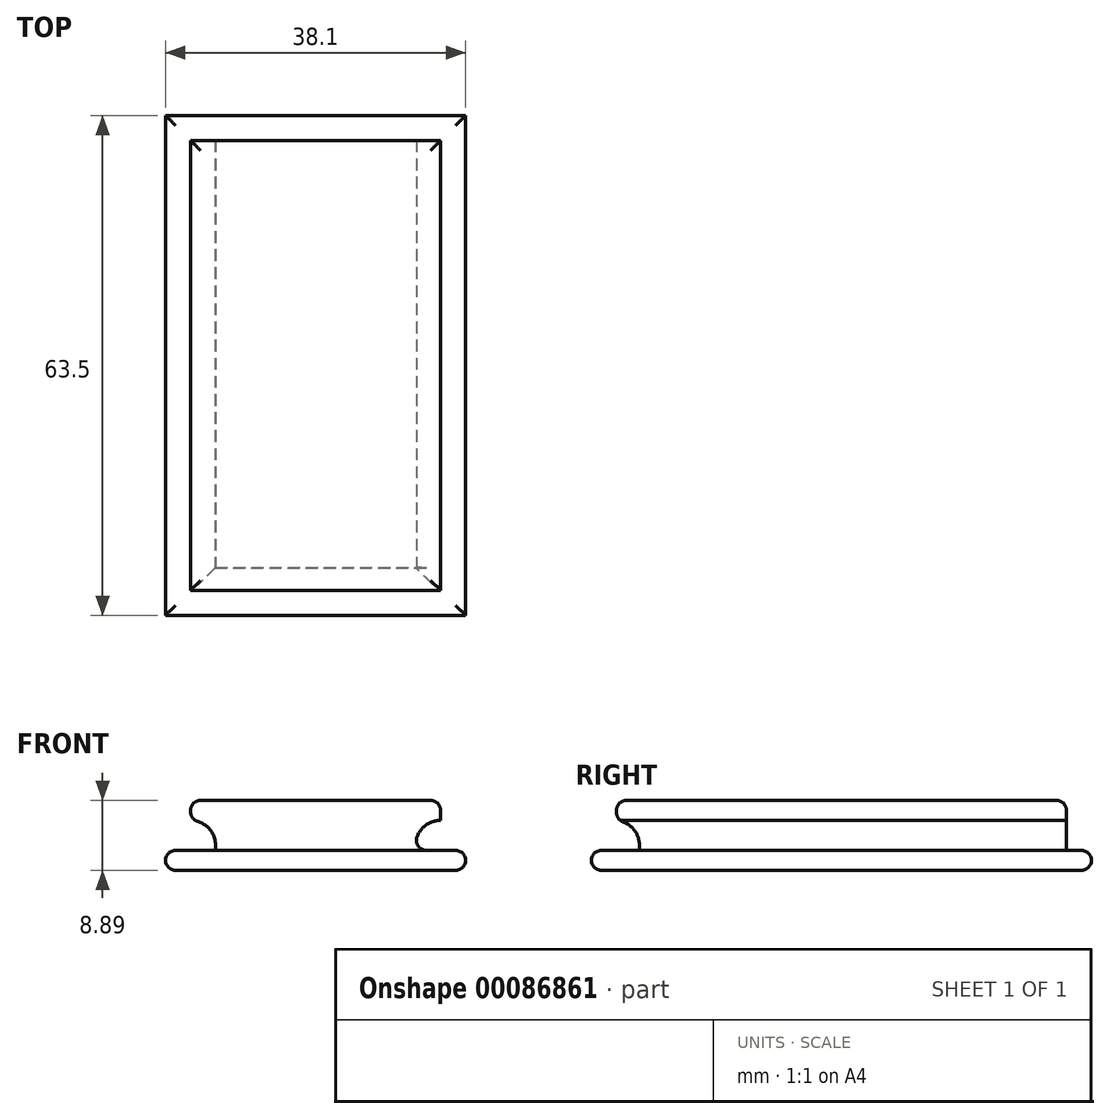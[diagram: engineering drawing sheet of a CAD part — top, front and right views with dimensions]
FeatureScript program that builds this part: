
annotation { "Feature Type Name" : "Feature", "Feature Type Description" : "" }
export const myFeature = defineFeature(function(context is Context, id is Id, definition is map)
    precondition{}
    {
        {
            var Q0;
            Q0=qCreatedBy(makeId("Top.planeOp"),FACE);
            var sketch = newSketch(context, id + "F0", { "sketchPlane" : qUnion([Q0])});
            skLineSegment(sketch, "E0.bottom", {"start": v(-25.4, 19.05) * mm, "end": v(25.4, 19.05) * mm});
            skLineSegment(sketch, "E0.top", {"start": v(-25.4, -19.05) * mm, "end": v(25.4, -19.05) * mm});
            skLineSegment(sketch, "E0.left", {"start": v(-31.75, 12.7) * mm, "end": v(-31.75, -12.7) * mm});
            skLineSegment(sketch, "E0.right", {"start": v(31.75, 12.7) * mm, "end": v(31.75, -12.7) * mm});
            skPoint(sketch, "E0.middle", {"position": v(0, 0) * mm});
            skPoint(sketch, "E1.visualSharp", {"position": v(-31.75, 19.05) * mm});
            skArc(sketch, "E1.filletArc", {"start": v(-25.4, 19.05) * mm, "mid": v(-29.9, 17.2) * mm, "end": v(-31.75, 12.7) * mm});
            skPoint(sketch, "E2.visualSharp", {"position": v(-31.75, -19.05) * mm});
            skArc(sketch, "E2.filletArc", {"start": v(-31.75, -12.7) * mm, "mid": v(-29.9, -17.2) * mm, "end": v(-25.4, -19.05) * mm});
            skPoint(sketch, "E3.visualSharp", {"position": v(31.75, 19.05) * mm});
            skArc(sketch, "E3.filletArc", {"start": v(31.75, 12.7) * mm, "mid": v(29.9, 17.2) * mm, "end": v(25.4, 19.05) * mm});
            skPoint(sketch, "E4.visualSharp", {"position": v(31.75, -19.05) * mm});
            skArc(sketch, "E4.filletArc", {"start": v(25.4, -19.05) * mm, "mid": v(29.9, -17.2) * mm, "end": v(31.75, -12.7) * mm});
            skSolve(sketch);
        }
        {
            var Q0;
            Q0=makeQuery(id+"F0.imprint","IMPRINT",FACE,{"disambiguationData":[TD([[makeQuery(id+"F0.imprint","IMPRINT",EDGE,{"derivedFrom":sQuery(id+"F0.wireOp",EDGE,"E0.bottom")}),-1.0]])]});
            extrude(context, id + "F1", {"entities" : qUnion([Q0]), "depth" : 7.62 * mm});
        }
        {
            var Q0;
            Q0=makeQuery(id+"F1.opExtrude","SWEPT_BODY",BODY,{"disambiguationData":[OSD([sQuery(id+"F0.wireOp",EDGE,"E0.bottom"),sQuery(id+"F0.wireOp",EDGE,"E0.top"),sQuery(id+"F0.wireOp",EDGE,"E0.left"),sQuery(id+"F0.wireOp",EDGE,"E0.right"),sQuery(id+"F0.wireOp",EDGE,"E1.filletArc"),sQuery(id+"F0.wireOp",EDGE,"E2.filletArc"),sQuery(id+"F0.wireOp",EDGE,"E3.filletArc"),sQuery(id+"F0.wireOp",EDGE,"E4.filletArc")])]});
            deleteBodies(context, id + "F2", {"entities" : qUnion([Q0])});
        }
        {
            var Q0;
            Q0=qCreatedBy(makeId("Top.planeOp"),FACE);
            var sketch = newSketch(context, id + "F3", { "sketchPlane" : qUnion([Q0])});
            skLineSegment(sketch, "E5.bottom", {"start": v(-15.87, 28.58) * mm, "end": v(15.88, 28.58) * mm});
            skLineSegment(sketch, "E5.top", {"start": v(-15.88, -28.58) * mm, "end": v(15.87, -28.58) * mm});
            skLineSegment(sketch, "E5.left", {"start": v(-15.87, 28.58) * mm, "end": v(-15.88, -28.58) * mm});
            skLineSegment(sketch, "E5.right", {"start": v(15.88, 28.58) * mm, "end": v(15.87, -28.58) * mm});
            skPoint(sketch, "E5.middle", {"position": v(0, 0) * mm});
            skSolve(sketch);
        }
        {
            var Q0;
            Q0=makeQuery(id+"F3.imprint","IMPRINT",FACE,{"disambiguationData":[TD([[makeQuery(id+"F3.imprint","IMPRINT",EDGE,{"derivedFrom":sQuery(id+"F3.wireOp",EDGE,"E5.bottom")}),-1.0]])]});
            extrude(context, id + "F4", {"entities" : qUnion([Q0]), "depth" : 6.35 * mm});
        }
        {
            var Q0;
            Q0=makeQuery(id+"F4.opExtrude","SWEPT_FACE",FACE,{"disambiguationData":[OSD([sQuery(id+"F3.wireOp",EDGE,"E5.top")])]});
            var sketch = newSketch(context, id + "F5", { "sketchPlane" : qUnion([Q0])});
            skCircle(sketch, "E6", {"center": v(15.87, 3.18) * mm, "radius": 3.18 * mm});
            skCircle(sketch, "E7.MirrorC", {"center": v(-15.87, 3.18) * mm, "radius": 3.18 * mm});
            skSolve(sketch);
        }
        {
            var Q0;
            {var subQ1=sQuery(id+"F3.wireOp",EDGE,"E5.top");var subQ2=makeQuery(id+"F4.opExtrude","SWEPT_EDGE",EDGE,{"disambiguationData":[OSD([subQ1,sQuery(id+"F3.wireOp",EDGE,"E5.left")])]});Q0=makeQuery(id+"F5.imprint","IMPRINT",FACE,{"disambiguationData":[TD([[makeQuery(id+"F5.imprint","IMPRINT",EDGE,{"derivedFrom":subQ2}),1.0]])]});}
            var Q1;
            {var subQ1=sQuery(id+"F3.wireOp",EDGE,"E5.top");var subQ2=makeQuery(id+"F4.opExtrude","SWEPT_EDGE",EDGE,{"disambiguationData":[OSD([subQ1,sQuery(id+"F3.wireOp",EDGE,"E5.right")])]});Q1=makeQuery(id+"F5.imprint","IMPRINT",FACE,{"disambiguationData":[TD([[makeQuery(id+"F5.imprint","IMPRINT",EDGE,{"derivedFrom":subQ2}),-1.0]])]});}
            extrude(context, id + "F6", {"entities" : qUnion([Q0, Q1]), "operationType" : NewBodyOperationType.REMOVE, "endBound" : BoundingType.THROUGH_ALL, "oppositeDirection" : true, "depth" : 25.4 * mm});
        }
        {
            var Q0;
            Q0=makeQuery(id+"F4.opExtrude","SWEPT_FACE",FACE,{"disambiguationData":[OSD([sQuery(id+"F3.wireOp",EDGE,"E5.left")])]});
            var sketch = newSketch(context, id + "F7", { "sketchPlane" : qUnion([Q0])});
            skSolve(sketch);
        }
        {
            var Q0;
            Q0=qCreatedBy(makeId("Right.planeOp"),FACE);
            cPlane(context, id + "F8", {"entities" : qUnion([Q0]), "cplaneType" : CPlaneType.OFFSET, "offset" : 152.4 * mm, "width" : 152.4 * mm, "height" : 152.4 * mm});
        }
        {
            var Q0;
            Q0=qCreatedBy(id+"F8.planeOp",FACE);
            var sketch = newSketch(context, id + "F9", { "sketchPlane" : qUnion([Q0])});
            skCircle(sketch, "E8", {"center": v(-28.83, 3.18) * mm, "radius": 3.17 * mm});
            skCircle(sketch, "E9.MirrorC", {"center": v(28.83, 3.18) * mm, "radius": 3.17 * mm});
            skSolve(sketch);
        }
        {
            var Q0;
            Q0=makeQuery(id+"F9.imprint","IMPRINT",FACE,{"disambiguationData":[TD([[makeQuery(id+"F9.imprint","IMPRINT",EDGE,{"derivedFrom":sQuery(id+"F9.wireOp",EDGE,"E8")}),1.0]])]});
            var Q1;
            Q1=makeQuery(id+"F9.imprint","IMPRINT",FACE,{"disambiguationData":[TD([[makeQuery(id+"F9.imprint","IMPRINT",EDGE,{"derivedFrom":sQuery(id+"F9.wireOp",EDGE,"E9.MirrorC")}),-1.0]])]});
            extrude(context, id + "F10", {"entities" : qUnion([Q0, Q1]), "operationType" : NewBodyOperationType.REMOVE, "endBound" : BoundingType.THROUGH_ALL, "oppositeDirection" : true, "depth" : 25.4 * mm});
        }
        {
            var Q0;
            Q0=qCreatedBy(makeId("Top.planeOp"),FACE);
            var sketch = newSketch(context, id + "F11", { "sketchPlane" : qUnion([Q0])});
            skLineSegment(sketch, "E10.bottom", {"start": v(-19.05, 31.75) * mm, "end": v(19.05, 31.75) * mm});
            skLineSegment(sketch, "E10.top", {"start": v(-19.05, -31.75) * mm, "end": v(19.05, -31.75) * mm});
            skLineSegment(sketch, "E10.left", {"start": v(-19.05, 31.75) * mm, "end": v(-19.05, -31.75) * mm});
            skLineSegment(sketch, "E10.right", {"start": v(19.05, 31.75) * mm, "end": v(19.05, -31.75) * mm});
            skPoint(sketch, "E10.middle", {"position": v(0, 0) * mm});
            skSolve(sketch);
        }
        {
            var Q0;
            Q0=makeQuery(id+"F11.imprint","IMPRINT",FACE,{"disambiguationData":[TD([[makeQuery(id+"F11.imprint","IMPRINT",EDGE,{"derivedFrom":sQuery(id+"F11.wireOp",EDGE,"E10.bottom")}),-1.0]])]});
            extrude(context, id + "F12", {"entities" : qUnion([Q0]), "operationType" : NewBodyOperationType.ADD, "depth" : 2.54 * mm});
        }
        {
            var Q0;
            Q0=makeQuery(id+"F4.opExtrude","CAP_FACE",FACE,{"disambiguationData":[OSD([sQuery(id+"F3.wireOp",EDGE,"E5.bottom"),sQuery(id+"F3.wireOp",EDGE,"E5.top"),sQuery(id+"F3.wireOp",EDGE,"E5.left"),sQuery(id+"F3.wireOp",EDGE,"E5.right")])],"isStart":false});
            extrude(context, id + "F13", {"entities" : qUnion([Q0]), "operationType" : NewBodyOperationType.ADD, "depth" : 2.54 * mm});
        }
        {
            var Q0;
            Q0=makeQuery(id+"F13.opExtrude","CAP_EDGE",EDGE,{"disambiguationData":[OSD([sQuery(id+"F3.wireOp",EDGE,"E5.top")])],"isStart":false});
            var Q1;
            Q1=makeQuery(id+"F10.boolean.opBoolean","INTERSECT",EDGE,{"disambiguationData":[OD(1.0)],"derivedFrom":[makeQuery(id+"F4.opExtrude","SWEPT_FACE",FACE,{"disambiguationData":[OSD([sQuery(id+"F3.wireOp",EDGE,"E5.top")])]}),makeQuery(id+"F10.opExtrude","SWEPT_FACE",FACE,{"disambiguationData":[OSD([sQuery(id+"F9.wireOp",EDGE,"E8")])]})]});
            var Q2;
            Q2=makeQuery(id+"F13.opExtrude","CAP_EDGE",EDGE,{"disambiguationData":[OSD([sQuery(id+"F3.wireOp",EDGE,"E5.top"),sQuery(id+"F3.wireOp",EDGE,"E5.right"),sQuery(id+"F5.wireOp",EDGE,"E6")])],"isStart":false});
            var Q3;
            Q3=makeQuery(id+"F12.boolean.opBoolean","INTERSECT",EDGE,{"derivedFrom":[makeQuery(id+"F6.boolean.opBoolean","COPY",FACE,{"derivedFrom":makeQuery(id+"F6.opExtrude","SWEPT_FACE",FACE,{"disambiguationData":[OSD([sQuery(id+"F5.wireOp",EDGE,"E6")])]})}),makeQuery(id+"F12.opExtrude","CAP_FACE",FACE,{"disambiguationData":[OSD([sQuery(id+"F11.wireOp",EDGE,"E10.bottom"),sQuery(id+"F11.wireOp",EDGE,"E10.top"),sQuery(id+"F11.wireOp",EDGE,"E10.left"),sQuery(id+"F11.wireOp",EDGE,"E10.right")])],"isStart":false})]});
            var Q4;
            Q4=makeQuery(id+"F13.opExtrude","CAP_EDGE",EDGE,{"disambiguationData":[OSD([sQuery(id+"F3.wireOp",EDGE,"E5.bottom")])],"isStart":false});
            var Q5;
            Q5=makeQuery(id+"F13.opExtrude","CAP_EDGE",EDGE,{"disambiguationData":[OSD([sQuery(id+"F3.wireOp",EDGE,"E5.top"),sQuery(id+"F3.wireOp",EDGE,"E5.left"),sQuery(id+"F5.wireOp",EDGE,"E7.MirrorC")])],"isStart":false});
            var Q6;
            Q6=makeQuery(id+"F12.opExtrude","CAP_EDGE",EDGE,{"disambiguationData":[OSD([sQuery(id+"F11.wireOp",EDGE,"E10.top")])],"isStart":false});
            var Q7;
            Q7=makeQuery(id+"F12.opExtrude","CAP_EDGE",EDGE,{"disambiguationData":[OSD([sQuery(id+"F11.wireOp",EDGE,"E10.right")])],"isStart":false});
            var Q8;
            Q8=makeQuery(id+"F12.opExtrude","CAP_EDGE",EDGE,{"disambiguationData":[OSD([sQuery(id+"F11.wireOp",EDGE,"E10.right")])],"isStart":true});
            var Q9;
            Q9=makeQuery(id+"F12.opExtrude","CAP_EDGE",EDGE,{"disambiguationData":[OSD([sQuery(id+"F11.wireOp",EDGE,"E10.top")])],"isStart":true});
            var Q10;
            {var subQ0=sQuery(id+"F5.wireOp",EDGE,"E7.MirrorC");var subQ1=sQuery(id+"F3.wireOp",EDGE,"E5.left");var subQ2=sQuery(id+"F3.wireOp",EDGE,"E5.top");Q10=makeQuery(id+"F13.boolean.opBoolean","MERGE",EDGE,{"derivedFrom":[makeQuery(id+"F6.boolean.opBoolean","MERGE",EDGE,{"derivedFrom":[makeQuery(id+"F4.opExtrude","CAP_EDGE",EDGE,{"disambiguationData":[OSD([subQ1])],"isStart":false}),makeQuery(id+"F6.opExtrude","SWEPT_EDGE",EDGE,{"disambiguationData":[OSD([subQ2,subQ1,subQ0]),TDD([makeQuery(id+"F5.imprint","INTERSECT",VERTEX,{"derivedFrom":[makeQuery(id+"F4.opExtrude","SWEPT_EDGE",EDGE,{"disambiguationData":[OSD([subQ2,subQ1])]}),makeQuery(id+"F4.opExtrude","CAP_EDGE",EDGE,{"disambiguationData":[OSD([subQ2])],"isStart":false}),subQ0]})])]})]}),makeQuery(id+"F13.opExtrude","CAP_EDGE",EDGE,{"disambiguationData":[OSD([subQ2,subQ1,subQ0])],"isStart":true})]});}
            var Q11;
            Q11=makeQuery(id+"F12.opExtrude","CAP_EDGE",EDGE,{"disambiguationData":[OSD([sQuery(id+"F11.wireOp",EDGE,"E10.left")])],"isStart":false});
            var Q12;
            Q12=makeQuery(id+"F12.opExtrude","CAP_EDGE",EDGE,{"disambiguationData":[OSD([sQuery(id+"F11.wireOp",EDGE,"E10.bottom")])],"isStart":true});
            var Q13;
            Q13=makeQuery(id+"F10.boolean.opBoolean","INTERSECT",EDGE,{"disambiguationData":[OD(1.0)],"derivedFrom":[makeQuery(id+"F4.opExtrude","SWEPT_FACE",FACE,{"disambiguationData":[OSD([sQuery(id+"F3.wireOp",EDGE,"E5.bottom")])]}),makeQuery(id+"F10.opExtrude","SWEPT_FACE",FACE,{"disambiguationData":[OSD([sQuery(id+"F9.wireOp",EDGE,"E9.MirrorC")])]})]});
            var Q14;
            Q14=makeQuery(id+"F12.opExtrude","CAP_EDGE",EDGE,{"disambiguationData":[OSD([sQuery(id+"F11.wireOp",EDGE,"E10.left")])],"isStart":true});
            var Q15;
            Q15=makeQuery(id+"F12.opExtrude","CAP_EDGE",EDGE,{"disambiguationData":[OSD([sQuery(id+"F11.wireOp",EDGE,"E10.bottom")])],"isStart":false});
            fillet(context, id + "F14", {"entities" : qUnion([Q0, Q1, Q2, Q3, Q4, Q5, Q6, Q7, Q8, Q9, Q10, Q11, Q12, Q13, Q14, Q15]), "radius" : 1.27 * mm, "tangentPropagation" : true, "allowEdgeOverflow" : false});
        }
    });
